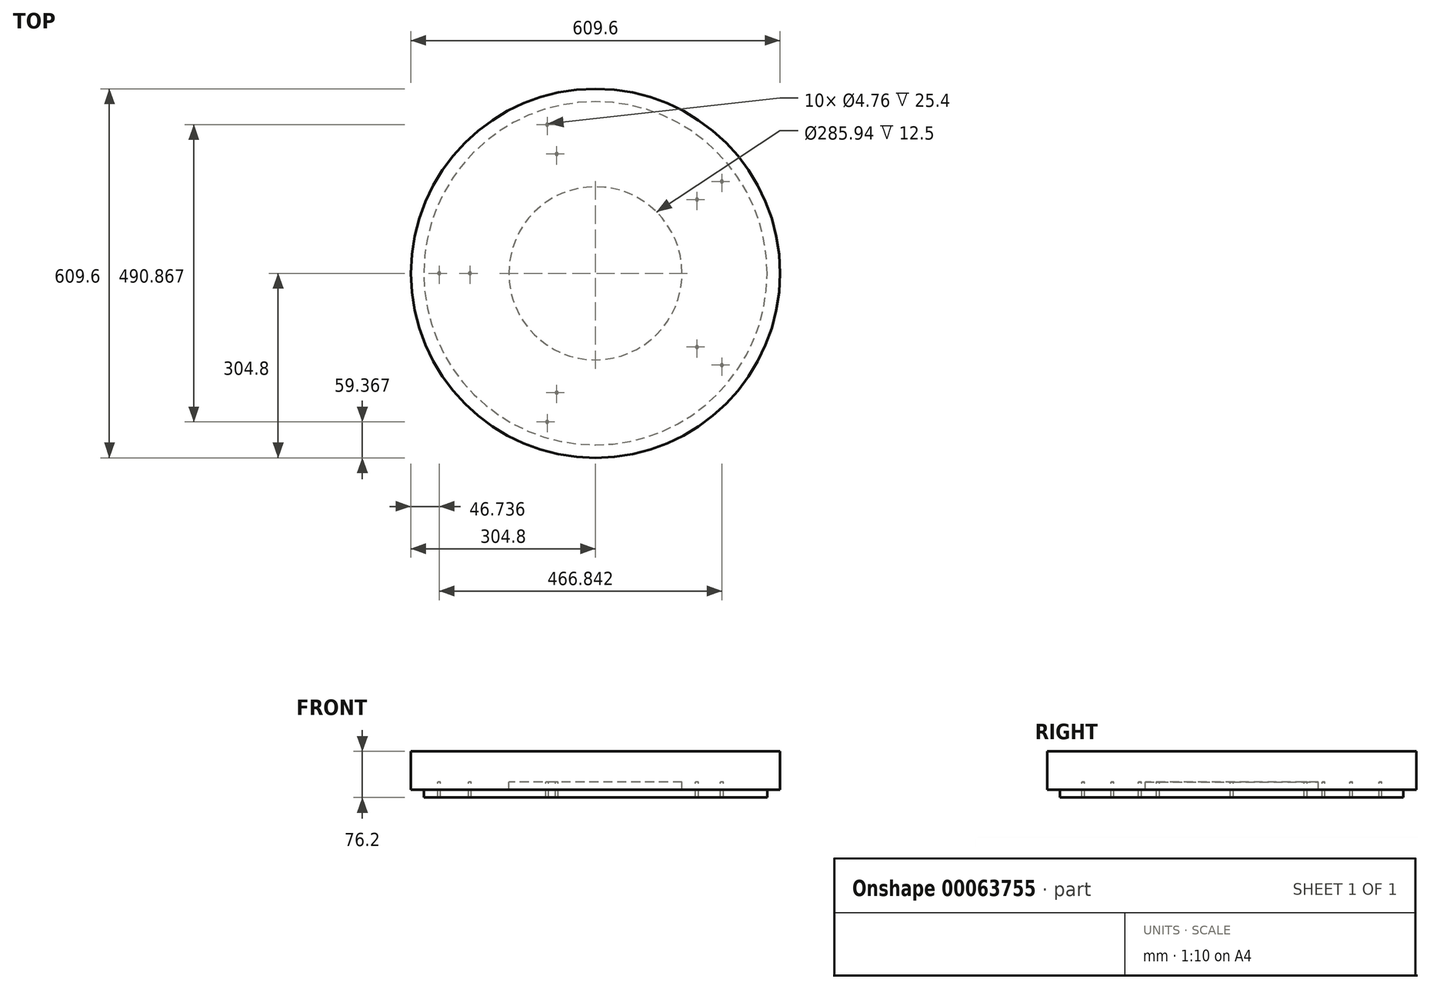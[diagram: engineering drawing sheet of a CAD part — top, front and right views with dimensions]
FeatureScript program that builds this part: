
annotation { "Feature Type Name" : "Feature", "Feature Type Description" : "" }
export const myFeature = defineFeature(function(context is Context, id is Id, definition is map)
    precondition{}
    {
        {
            assignVariable(context, id + "F0", {"name" : "H", "anyValue" : 18});
        }
        {
            assignVariable(context, id + "F1", {"name" : "S", "anyValue" : 5});
        }
        {
            var Q0;
            Q0=qCreatedBy(makeId("Top.planeOp"),FACE);
            var sketch = newSketch(context, id + "F2", { "sketchPlane" : qUnion([Q0])});
            skCircle(sketch, "E0", {"center": v(0, 0) * mm, "radius": 304.8 * mm});
            skCircle(sketch, "E1", {"center": v(0, 0) * mm, "radius": 292.1 * mm});
            skCircle(sketch, "E2.0", {"center": v(0, 0) * mm, "radius": 283.46 * mm});
            skSolve(sketch);
        }
        {
            var Q0;
            Q0=makeQuery(id+"F2.imprint","IMPRINT",FACE,{"disambiguationData":[TD([[makeQuery(id+"F2.imprint","IMPRINT",EDGE,{"derivedFrom":sQuery(id+"F2.wireOp",EDGE,"E1")}),1.0]])]});
            var Q1;
            Q1=sQuery(id+"F2.wireOp",EDGE,"E1");
            var Q2;
            Q2=sQuery(id+"F2.wireOp",EDGE,"E2.0");
            extrude(context, id + "F3", {"entities" : qUnion([Q0]), "surfaceEntities" : qUnion([Q1, Q2]), "depth" : (getVariable(context, 'H') - 5.5) * mm});
        }
        {
            var Q0;
            Q0=makeQuery(id+"F3.opExtrude","CAP_FACE",FACE,{"disambiguationData":[OSD([sQuery(id+"F2.wireOp",EDGE,"E1"),sQuery(id+"F2.wireOp",EDGE,"E2.0")])],"isStart":false});
            var sketch = newSketch(context, id + "F4", { "sketchPlane" : qUnion([Q0])});
            skCircle(sketch, "E3.0", {"center": v(0, 0) * mm, "radius": 283.46 * mm});
            skSolve(sketch);
        }
        {
            var Q0;
            Q0 = qSketchRegion(id + "F4", true);
            extrude(context, id + "F5", {"entities" : qUnion([Q0]), "oppositeDirection" : true, "depth" : 25.4 * mm});
        }
        {
            var Q0;
            Q0=makeQuery(id+"F5.opExtrude","CAP_FACE",FACE,{"disambiguationData":[OSD([sQuery(id+"F4.wireOp",EDGE,"E3.0")])],"isStart":true});
            var sketch = newSketch(context, id + "F6", { "sketchPlane" : qUnion([Q0])});
            skLineSegment(sketch, "E4", {"start": v(-283.46, 0) * mm, "end": v(0, 0) * mm, "construction": true});
            skCircle(sketch, "E5.0", {"center": v(0, 0) * mm, "radius": 258.06 * mm, "construction": true});
            skCircle(sketch, "E6.0", {"center": v(0, 0) * mm, "radius": 207.26 * mm, "construction": true});
            skPoint(sketch, "E7", {"position": v(-258.06, 0) * mm});
            skPoint(sketch, "E8", {"position": v(-207.26, 0) * mm});
            skPoint(sketch, "E9.1.0", {"position": v(-64.05, -197.12) * mm});
            skPoint(sketch, "E9.1.1", {"position": v(-79.75, -245.43) * mm});
            skPoint(sketch, "E9.2.0", {"position": v(167.68, -121.83) * mm});
            skPoint(sketch, "E9.2.1", {"position": v(208.78, -151.69) * mm});
            skPoint(sketch, "E9.3.0", {"position": v(167.68, 121.83) * mm});
            skPoint(sketch, "E9.3.1", {"position": v(208.78, 151.69) * mm});
            skPoint(sketch, "E9.4.0", {"position": v(-64.05, 197.12) * mm});
            skPoint(sketch, "E9.4.1", {"position": v(-79.75, 245.43) * mm});
            skSolve(sketch);
        }
        {
            var Q0;
            Q0=sQuery(id+"F6.wireOp",VERTEX,"E7");
            var Q1;
            Q1=sQuery(id+"F6.wireOp",VERTEX,"E8");
            var Q2;
            Q2=sQuery(id+"F6.wireOp",VERTEX,"E9.4.1");
            var Q3;
            Q3=sQuery(id+"F6.wireOp",VERTEX,"E9.4.0");
            var Q4;
            Q4=sQuery(id+"F6.wireOp",VERTEX,"E9.3.0");
            var Q5;
            Q5=sQuery(id+"F6.wireOp",VERTEX,"E9.3.1");
            var Q6;
            Q6=sQuery(id+"F6.wireOp",VERTEX,"E9.2.0");
            var Q7;
            Q7=sQuery(id+"F6.wireOp",VERTEX,"E9.2.1");
            var Q8;
            Q8=sQuery(id+"F6.wireOp",VERTEX,"E9.1.1");
            var Q9;
            Q9=sQuery(id+"F6.wireOp",VERTEX,"E9.1.0");
            var Q10;
            Q10=sQuery(id+"F6.wireOp",VERTEX,"58d6160c-07d9-473b-a502-2546abea6cd9.1.6.0");
            var Q11;
            Q11=sQuery(id+"F6.wireOp",VERTEX,"58d6160c-07d9-473b-a502-2546abea6cd9.0.6.0");
            var Q12;
            Q12=sQuery(id+"F6.wireOp",VERTEX,"58d6160c-07d9-473b-a502-2546abea6cd9.0.5.0");
            var Q13;
            Q13=sQuery(id+"F6.wireOp",VERTEX,"58d6160c-07d9-473b-a502-2546abea6cd9.1.5.0");
            var Q14;
            Q14=makeQuery(id+"F5.opExtrude","SWEPT_BODY",BODY,{"disambiguationData":[OSD([sQuery(id+"F4.wireOp",EDGE,"E3.0")])]});
            hole(context, id + "F7", {"style" : HoleStyle.C_SINK, "holeDiameter" : 4.76 * mm, "cSinkDiameter" : 8.43 * mm, "endStyle" : HoleEndStyle.THROUGH, "locations" : qUnion([Q0, Q1, Q2, Q3, Q4, Q5, Q6, Q7, Q8, Q9, Q10, Q11, Q12, Q13]), "scope" : qUnion([Q14]), "cSinkAngle" : 90 * degree});
        }
        {
            var Q0;
            Q0=makeQuery(id+"F5.opExtrude","SWEPT_BODY",BODY,{"disambiguationData":[OSD([sQuery(id+"F4.wireOp",EDGE,"E3.0")])]});
            var Q1;
            Q1=qCreatedBy(makeId("Top.planeOp"),FACE);
            mirror(context, id + "F8", {"entities" : qUnion([Q0]), "mirrorPlane" : qUnion([Q1])});
        }
        {
            var Q0;
            Q0=makeQuery(id+"F8.opPattern","COPY",BODY,{"derivedFrom":makeQuery(id+"F5.opExtrude","SWEPT_BODY",BODY,{"disambiguationData":[OSD([sQuery(id+"F4.wireOp",EDGE,"E3.0")])]}),"instanceName":"1"});
            var Q1;
            Q1=makeQuery(id+"F5.opExtrude","CAP_FACE",FACE,{"disambiguationData":[OSD([sQuery(id+"F4.wireOp",EDGE,"E3.0")])],"isStart":true});
            transform(context, id + "F9", {"entities" : qUnion([Q0]), "transformType" : TransformType.TRANSLATION_3D, "dx" : 0 * mm, "dy" : 0 * mm, "dz" : (getVariable(context, 'H') - 5.5) * mm, "makeCopy" : false});
        }
        {
            var Q0;
            Q0=makeQuery(id+"F8.opPattern","COPY",FACE,{"derivedFrom":makeQuery(id+"F5.opExtrude","CAP_FACE",FACE,{"disambiguationData":[OSD([sQuery(id+"F4.wireOp",EDGE,"E3.0")])],"isStart":true}),"instanceName":"1"});
            var sketch = newSketch(context, id + "F10", { "sketchPlane" : qUnion([Q0])});
            skCircle(sketch, "E10.0", {"center": v(0, 0) * mm, "radius": 265.2 * mm, "construction": true});
            skCircle(sketch, "E11.0", {"center": v(0, 0) * mm, "radius": 228.7 * mm, "construction": true});
            skCircle(sketch, "E12.0", {"center": v(0, 0) * mm, "radius": 192.18 * mm, "construction": true});
            skLineSegment(sketch, "E13", {"start": v(0, 0) * mm, "end": v(0, 265.2) * mm, "construction": true});
            skLineSegment(sketch, "E14.0", {"start": v(22.23, 0) * mm, "end": v(22.23, 265.2) * mm, "construction": true});
            skLineSegment(sketch, "E15.0", {"start": v(-22.23, 0) * mm, "end": v(-22.23, 265.2) * mm, "construction": true});
            skPoint(sketch, "E16", {"position": v(-22.23, 227.61) * mm});
            skPoint(sketch, "E17", {"position": v(-22.23, 190.9) * mm});
            skPoint(sketch, "E18", {"position": v(22.23, 190.9) * mm});
            skPoint(sketch, "E19", {"position": v(22.23, 227.61) * mm});
            skPoint(sketch, "E20", {"position": v(22.23, 264.27) * mm});
            skPoint(sketch, "E21", {"position": v(-22.23, 264.27) * mm});
            skPoint(sketch, "E22.1.0", {"position": v(-188.42, 37.85) * mm});
            skPoint(sketch, "E22.1.1", {"position": v(-223.34, 49.2) * mm});
            skPoint(sketch, "E22.1.2", {"position": v(-258.2, 60.53) * mm});
            skPoint(sketch, "E22.1.3", {"position": v(-244.47, 102.8) * mm});
            skPoint(sketch, "E22.1.4", {"position": v(-209.6, 91.47) * mm});
            skPoint(sketch, "E22.1.5", {"position": v(-174.68, 80.13) * mm});
            skPoint(sketch, "E22.2.0", {"position": v(-94.22, -167.5) * mm});
            skPoint(sketch, "E22.2.1", {"position": v(-115.8, -197.2) * mm});
            skPoint(sketch, "E22.2.2", {"position": v(-137.36, -226.87) * mm});
            skPoint(sketch, "E22.2.3", {"position": v(-173.32, -200.74) * mm});
            skPoint(sketch, "E22.2.4", {"position": v(-151.77, -171.08) * mm});
            skPoint(sketch, "E22.2.5", {"position": v(-130.18, -141.37) * mm});
            skPoint(sketch, "E22.3.0", {"position": v(130.18, -141.37) * mm});
            skPoint(sketch, "E22.3.1", {"position": v(151.77, -171.08) * mm});
            skPoint(sketch, "E22.3.2", {"position": v(173.32, -200.74) * mm});
            skPoint(sketch, "E22.3.3", {"position": v(137.36, -226.87) * mm});
            skPoint(sketch, "E22.3.4", {"position": v(115.8, -197.2) * mm});
            skPoint(sketch, "E22.3.5", {"position": v(94.22, -167.5) * mm});
            skPoint(sketch, "E22.4.0", {"position": v(174.68, 80.13) * mm});
            skPoint(sketch, "E22.4.1", {"position": v(209.6, 91.47) * mm});
            skPoint(sketch, "E22.4.2", {"position": v(244.47, 102.8) * mm});
            skPoint(sketch, "E22.4.3", {"position": v(258.2, 60.53) * mm});
            skPoint(sketch, "E22.4.4", {"position": v(223.34, 49.2) * mm});
            skPoint(sketch, "E22.4.5", {"position": v(188.42, 37.85) * mm});
            skSolve(sketch);
        }
        {
            var Q0;
            Q0=sQuery(id+"F10.wireOp",VERTEX,"E21");
            var Q1;
            Q1=sQuery(id+"F10.wireOp",VERTEX,"E16");
            var Q2;
            Q2=sQuery(id+"F10.wireOp",VERTEX,"E17");
            var Q3;
            Q3=sQuery(id+"F10.wireOp",VERTEX,"E18");
            var Q4;
            Q4=sQuery(id+"F10.wireOp",VERTEX,"E19");
            var Q5;
            Q5=sQuery(id+"F10.wireOp",VERTEX,"E20");
            var Q6;
            Q6=sQuery(id+"F10.wireOp",VERTEX,"E22.4.0");
            var Q7;
            Q7=sQuery(id+"F10.wireOp",VERTEX,"E22.4.1");
            var Q8;
            Q8=sQuery(id+"F10.wireOp",VERTEX,"E22.4.2");
            var Q9;
            Q9=sQuery(id+"F10.wireOp",VERTEX,"E22.4.3");
            var Q10;
            Q10=sQuery(id+"F10.wireOp",VERTEX,"E22.4.4");
            var Q11;
            Q11=sQuery(id+"F10.wireOp",VERTEX,"E22.4.5");
            var Q12;
            Q12=sQuery(id+"F10.wireOp",VERTEX,"E22.3.0");
            var Q13;
            Q13=sQuery(id+"F10.wireOp",VERTEX,"E22.3.1");
            var Q14;
            Q14=sQuery(id+"F10.wireOp",VERTEX,"E22.3.2");
            var Q15;
            Q15=sQuery(id+"F10.wireOp",VERTEX,"E22.3.3");
            var Q16;
            Q16=sQuery(id+"F10.wireOp",VERTEX,"E22.3.4");
            var Q17;
            Q17=sQuery(id+"F10.wireOp",VERTEX,"E22.3.5");
            var Q18;
            Q18=sQuery(id+"F10.wireOp",VERTEX,"E22.2.2");
            var Q19;
            Q19=sQuery(id+"F10.wireOp",VERTEX,"E22.2.1");
            var Q20;
            Q20=sQuery(id+"F10.wireOp",VERTEX,"E22.2.0");
            var Q21;
            Q21=sQuery(id+"F10.wireOp",VERTEX,"E22.2.5");
            var Q22;
            Q22=sQuery(id+"F10.wireOp",VERTEX,"E22.2.4");
            var Q23;
            Q23=sQuery(id+"F10.wireOp",VERTEX,"E22.2.3");
            var Q24;
            Q24=sQuery(id+"F10.wireOp",VERTEX,"E22.1.0");
            var Q25;
            Q25=sQuery(id+"F10.wireOp",VERTEX,"E22.1.5");
            var Q26;
            Q26=sQuery(id+"F10.wireOp",VERTEX,"E22.1.1");
            var Q27;
            Q27=sQuery(id+"F10.wireOp",VERTEX,"E22.1.2");
            var Q28;
            Q28=sQuery(id+"F10.wireOp",VERTEX,"E22.1.3");
            var Q29;
            Q29=sQuery(id+"F10.wireOp",VERTEX,"E22.1.4");
            var Q30;
            Q30=makeQuery(id+"F8.opPattern","COPY",BODY,{"derivedFrom":makeQuery(id+"F5.opExtrude","SWEPT_BODY",BODY,{"disambiguationData":[OSD([sQuery(id+"F4.wireOp",EDGE,"E3.0")])]}),"instanceName":"1"});
            hole(context, id + "F11", {"style" : HoleStyle.SIMPLE, "holeDiameter" : 3.17 * mm, "endStyle" : HoleEndStyle.BLIND, "holeDepth" : 3.17 * mm, "locations" : qUnion([Q0, Q1, Q2, Q3, Q4, Q5, Q6, Q7, Q8, Q9, Q10, Q11, Q12, Q13, Q14, Q15, Q16, Q17, Q18, Q19, Q20, Q21, Q22, Q23, Q24, Q25, Q26, Q27, Q28, Q29]), "scope" : qUnion([Q30])});
        }
        {
            var Q0;
            Q0=makeQuery(id+"F8.opPattern","COPY",FACE,{"derivedFrom":makeQuery(id+"F5.opExtrude","CAP_FACE",FACE,{"disambiguationData":[OSD([sQuery(id+"F4.wireOp",EDGE,"E3.0")])],"isStart":false}),"instanceName":"1"});
            var sketch = newSketch(context, id + "F12", { "sketchPlane" : qUnion([Q0])});
            skCircle(sketch, "E23", {"center": v(0, 0) * mm, "radius": 142.97 * mm});
            skSolve(sketch);
        }
        {
            var Q0;
            Q0 = qSketchRegion(id + "F12", true);
            extrude(context, id + "F13", {"entities" : qUnion([Q0]), "operationType" : NewBodyOperationType.REMOVE, "oppositeDirection" : true, "depth" : 25.4 * mm});
        }
        {
            var Q0;
            Q0=makeQuery(id+"F8.opPattern","COPY",FACE,{"derivedFrom":makeQuery(id+"F5.opExtrude","CAP_FACE",FACE,{"disambiguationData":[OSD([sQuery(id+"F4.wireOp",EDGE,"E3.0")])],"isStart":false}),"instanceName":"1"});
            var sketch = newSketch(context, id + "F14", { "sketchPlane" : qUnion([Q0])});
            skLineSegment(sketch, "E24", {"start": v(-258.06, 0) * mm, "end": v(-207.26, 0) * mm, "construction": true});
            skLineSegment(sketch, "E25.0", {"start": v(-283.46, 12.7) * mm, "end": v(-181.86, 12.7) * mm});
            skLineSegment(sketch, "E26.0", {"start": v(-283.46, -12.7) * mm, "end": v(-181.86, -12.7) * mm});
            skLineSegment(sketch, "E27", {"start": v(-283.46, -12.7) * mm, "end": v(-283.46, 12.7) * mm});
            skLineSegment(sketch, "E28", {"start": v(-181.86, -12.7) * mm, "end": v(-181.86, 12.7) * mm});
            skSolve(sketch);
        }
        {
            var Q0;
            Q0 = qSketchRegion(id + "F14", true);
            extrude(context, id + "F15", {"entities" : qUnion([Q0]), "depth" : (getVariable(context, 'H') - 7.5) * mm});
        }
        {
            var Q0;
            Q0=makeQuery(id+"F15.opExtrude","SWEPT_BODY",BODY,{"disambiguationData":[OSD([sQuery(id+"F14.wireOp",EDGE,"E25.0"),sQuery(id+"F14.wireOp",EDGE,"E26.0"),sQuery(id+"F14.wireOp",EDGE,"E27"),sQuery(id+"F14.wireOp",EDGE,"E28")])]});
            var Q1;
            Q1=makeQuery(id+"F8.opPattern","COPY",EDGE,{"derivedFrom":makeQuery(id+"F5.opExtrude","CAP_EDGE",EDGE,{"disambiguationData":[OSD([sQuery(id+"F4.wireOp",EDGE,"E3.0")])],"isStart":false}),"instanceName":"1"});
            circularPattern(context, id + "F16", {"entities" : qUnion([Q0]), "axis" : qUnion([Q1]), "angle" : 360 * degree, "instanceCount" : getVariable(context, 'S'), "equalSpace" : true});
        }
        {
            var Q0;
            Q0=makeQuery(id+"F2.imprint","IMPRINT",FACE,{"disambiguationData":[TD([[makeQuery(id+"F2.imprint","IMPRINT",EDGE,{"derivedFrom":sQuery(id+"F2.wireOp",EDGE,"E0")}),1.0]])]});
            extrude(context, id + "F17", {"entities" : qUnion([Q0]), "depth" : (getVariable(context, 'H') - 5.5) * mm});
        }
        {
            var Q0;
            Q0=makeQuery(id+"F17.opExtrude","CAP_FACE",FACE,{"disambiguationData":[OSD([sQuery(id+"F2.wireOp",EDGE,"E0"),sQuery(id+"F2.wireOp",EDGE,"E1")])],"isStart":false});
            var sketch = newSketch(context, id + "F18", { "sketchPlane" : qUnion([Q0])});
            skCircle(sketch, "E29.0", {"center": v(0, 0) * mm, "radius": 304.8 * mm});
            skSolve(sketch);
        }
        {
            var Q0;
            Q0 = qSketchRegion(id + "F18", true);
            extrude(context, id + "F19", {"entities" : qUnion([Q0]), "operationType" : NewBodyOperationType.ADD, "depth" : 50.8 * mm});
        }
    });
